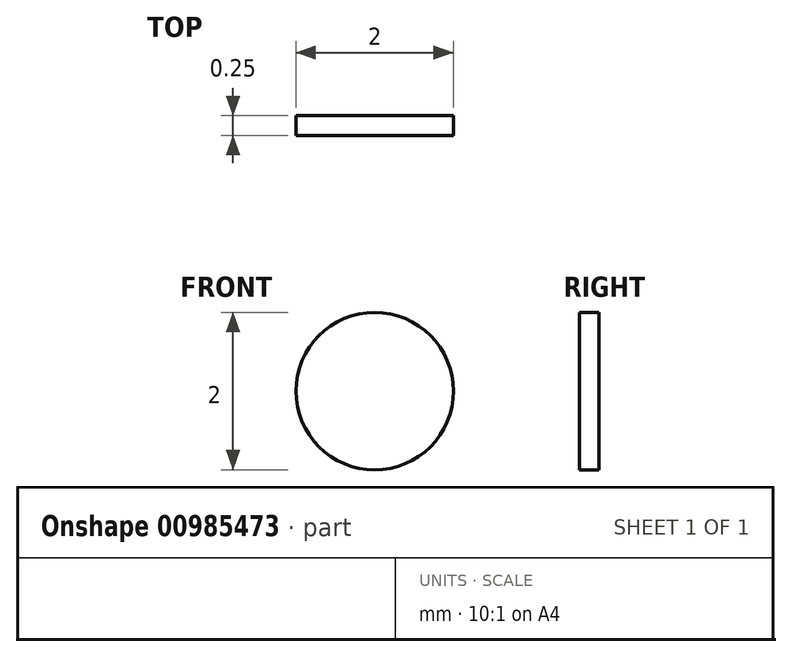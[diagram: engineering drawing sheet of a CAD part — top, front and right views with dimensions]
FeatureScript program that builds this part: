
annotation { "Feature Type Name" : "Feature", "Feature Type Description" : "" }
export const myFeature = defineFeature(function(context is Context, id is Id, definition is map)
    precondition{}
    {
        {
            var Q0;
            Q0=qCreatedBy(makeId("Front.planeOp"),FACE);
            var sketch = newSketch(context, id + "F0", { "sketchPlane" : qUnion([Q0])});
            skCircle(sketch, "E0", {"center": v(0, 0) * mm, "radius": 1 * mm});
            skSolve(sketch);
        }
        {
            var Q0;
            Q0=qSketchRegion(id+"F0",true);
            extrude(context, id + "F1", {"entities" : qUnion([Q0]), "depth" : .25 * mm});
        }
    });
